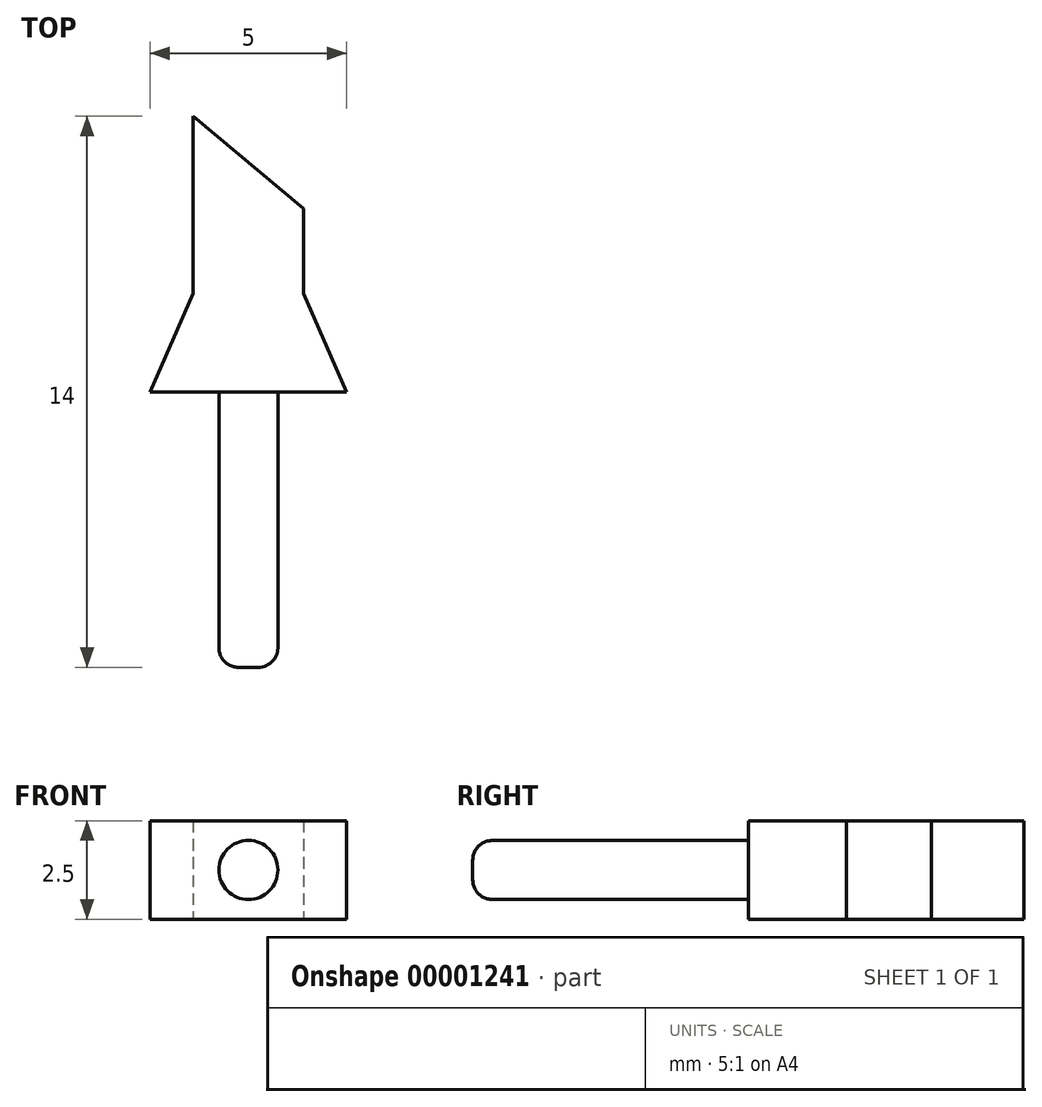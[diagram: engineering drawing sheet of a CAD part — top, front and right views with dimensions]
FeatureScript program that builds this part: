
annotation { "Feature Type Name" : "Feature", "Feature Type Description" : "" }
export const myFeature = defineFeature(function(context is Context, id is Id, definition is map)
    precondition{}
    {
        {
            var Q0;
            Q0=qCreatedBy(makeId("Top.planeOp"),FACE);
            var sketch = newSketch(context, id + "F0", { "sketchPlane" : qUnion([Q0])});
            skLineSegment(sketch, "E0", {"start": v(0, 0) * mm, "end": v(0, 4.5) * mm});
            skLineSegment(sketch, "E1", {"start": v(0, 4.5) * mm, "end": v(2.8, 2.15) * mm});
            skLineSegment(sketch, "E2", {"start": v(2.8, 2.15) * mm, "end": v(2.8, 0) * mm});
            skLineSegment(sketch, "E3", {"start": v(2.8, 0) * mm, "end": v(3.9, -2.5) * mm});
            skLineSegment(sketch, "E4", {"start": v(3.9, -2.5) * mm, "end": v(2.8, -2.5) * mm});
            skLineSegment(sketch, "E5", {"start": v(2.8, -2.5) * mm, "end": v(2.8, -5.5) * mm});
            skLineSegment(sketch, "E6", {"start": v(2.8, -5.5) * mm, "end": v(0, -5.5) * mm});
            skLineSegment(sketch, "E7", {"start": v(0, -5.5) * mm, "end": v(0, -2.5) * mm});
            skLineSegment(sketch, "E8", {"start": v(0, -2.5) * mm, "end": v(-1.1, -2.5) * mm});
            skLineSegment(sketch, "E9", {"start": v(-1.1, -2.5) * mm, "end": v(0, 0) * mm});
            skLineSegment(sketch, "E10", {"start": v(1.4, 3.33) * mm, "end": v(1.4, -5.5) * mm, "construction": true});
            skLineSegment(sketch, "E11", {"start": v(-1.1, -2.5) * mm, "end": v(3.9, -2.5) * mm, "construction": true});
            skPoint(sketch, "E12", {"position": v(1.4, -2.5) * mm});
            skLineSegment(sketch, "E13", {"start": v(0, -2.5) * mm, "end": v(2.8, -2.5) * mm});
            skSolve(sketch);
        }
        {
            var Q0;
            Q0=makeQuery(id+"F0.imprint","IMPRINT",FACE,{"disambiguationData":[TD([[makeQuery(id+"F0.imprint","IMPRINT",EDGE,{"derivedFrom":sQuery(id+"F0.wireOp",EDGE,"E0")}),-1.0]])]});
            extrude(context, id + "F1", {"entities" : qUnion([Q0]), "depth" : 2.5 * mm});
        }
        {
            var Q0;
            Q0=makeQuery(id+"F1.opExtrude","SWEPT_FACE",FACE,{"disambiguationData":[OSD([sQuery(id+"F0.wireOp",EDGE,"E4"),sQuery(id+"F0.wireOp",EDGE,"E8"),sQuery(id+"F0.wireOp",EDGE,"E13")])]});
            var sketch = newSketch(context, id + "F2", { "sketchPlane" : qUnion([Q0])});
            skLineSegment(sketch, "E14", {"start": v(-1.1, 2.5) * mm, "end": v(3.9, 0) * mm, "construction": true});
            skCircle(sketch, "E15", {"center": v(1.4, 1.25) * mm, "radius": 0.75 * mm});
            skSolve(sketch);
        }
        {
            var Q0;
            Q0=makeQuery(id+"F2.imprint","IMPRINT",FACE,{"disambiguationData":[TD([[makeQuery(id+"F2.imprint","IMPRINT",EDGE,{"derivedFrom":sQuery(id+"F2.wireOp",EDGE,"E15")}),1.0]])]});
            extrude(context, id + "F3", {"entities" : qUnion([Q0]), "operationType" : NewBodyOperationType.ADD, "depth" : 7 * mm});
        }
        {
            var Q0;
            Q0=makeQuery(id+"F3.opExtrude","CAP_EDGE",EDGE,{"disambiguationData":[OSD([sQuery(id+"F2.wireOp",EDGE,"E15")])],"isStart":false});
            var Q1;
            Q1=makeQuery(id+"F3.opExtrude","CAP_EDGE",EDGE,{"disambiguationData":[OSD([sQuery(id+"F2.wireOp",EDGE,"E15")])],"isStart":true});
            fillet(context, id + "F4", {"entities" : qUnion([Q0, Q1]), "radius" : 0.5 * mm, "tangentPropagation" : true, "allowEdgeOverflow" : false});
        }
    });
